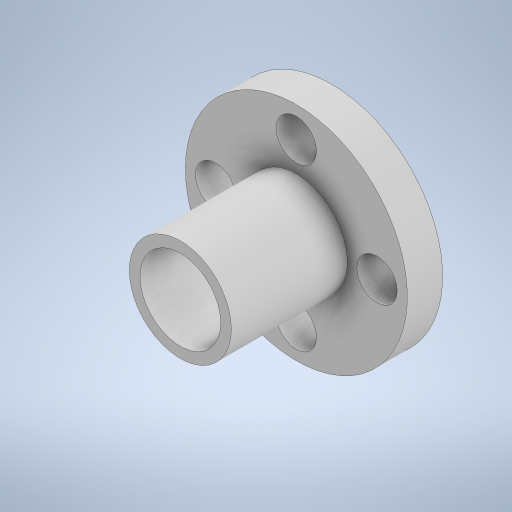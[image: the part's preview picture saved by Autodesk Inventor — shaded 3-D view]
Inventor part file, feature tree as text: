
AUTODESK INVENTOR PART (.ipt)
format: ipt  version: 2024 (Build 280153000, 153)  size: 266,752 bytes
history: native  units: in
note: dims shown in document units (in); Inventor stores cm internally (conversion verified against a paired STEP export)
features: extrude x2, sketch x2
ambient origin geometry x8: Origin, YZ Plane, XZ Plane, XY Plane, X Axis, Y Axis, Z Axis, Center Point
bodies: Solid1 (feature_tree)
feature tree (4):
  extrude  "Extrusion1"  Depth=0.315in
  extrude  "Extrusion2"  Depth=0.1378in
  sketch  "Sketch1"  dims[d0=0.3984in d1=0.315in]
  sketch  "Sketch2"  dims[d2=0.5906in d3=0.0in d4=0.8661in d5=0.315in d6=0.1575in d7=0.1575in d8=0.1575in d9=0.1575in d10=0.1378in d11=0.0in]
